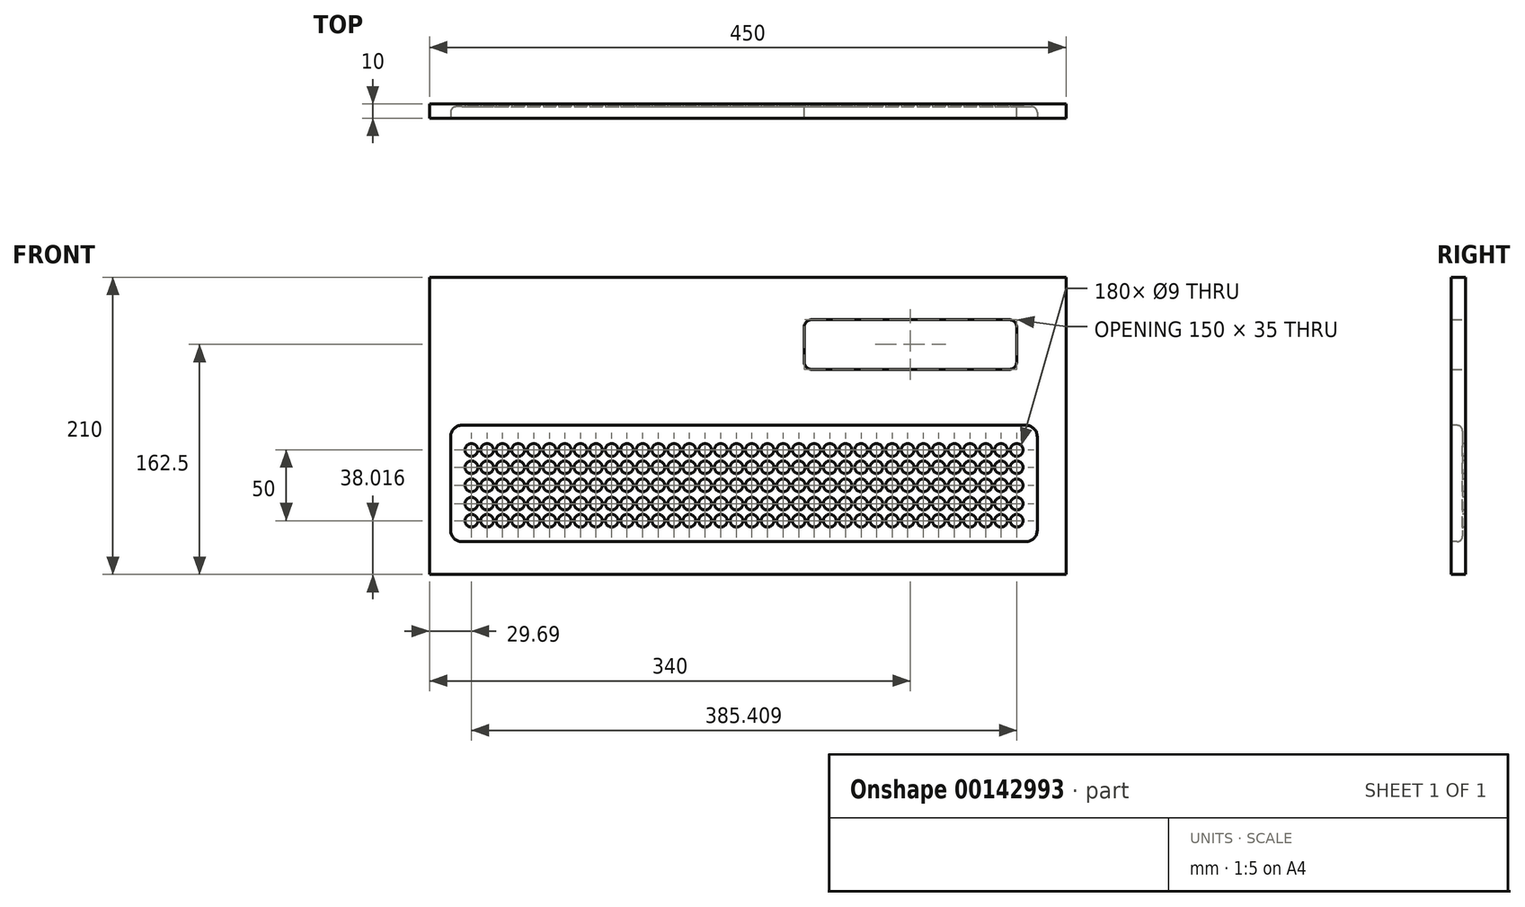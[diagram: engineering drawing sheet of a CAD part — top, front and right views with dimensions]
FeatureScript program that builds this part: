
annotation { "Feature Type Name" : "Feature", "Feature Type Description" : "" }
export const myFeature = defineFeature(function(context is Context, id is Id, definition is map)
    precondition{}
    {
        {
            var Q0;
            Q0=qCreatedBy(makeId("Front.planeOp"),FACE);
            var sketch = newSketch(context, id + "F0", { "sketchPlane" : qUnion([Q0])});
            skLineSegment(sketch, "E0.bottom", {"start": v(0, 0) * mm, "end": v(450, 0) * mm});
            skLineSegment(sketch, "E0.left", {"start": v(0, 0) * mm, "end": v(0, 210) * mm});
            skLineSegment(sketch, "E0.right", {"start": v(450, 0) * mm, "end": v(450, 210) * mm});
            skLineSegment(sketch, "E1.bottom", {"start": v(450, 210) * mm, "end": v(265, 210) * mm});
            skLineSegment(sketch, "E1.top", {"start": v(450, 145) * mm, "end": v(265, 145) * mm, "construction": true});
            skLineSegment(sketch, "E1.right", {"start": v(265, 210) * mm, "end": v(265, 145) * mm, "construction": true});
            skLineSegment(sketch, "E2", {"start": v(0, 210) * mm, "end": v(265, 210) * mm});
            skLineSegment(sketch, "E3.bottom", {"start": v(270, 145) * mm, "end": v(410, 145) * mm});
            skLineSegment(sketch, "E3.top", {"start": v(270, 180) * mm, "end": v(410, 180) * mm});
            skLineSegment(sketch, "E3.left", {"start": v(265, 150) * mm, "end": v(265, 175) * mm});
            skLineSegment(sketch, "E3.right", {"start": v(415, 150) * mm, "end": v(415, 175) * mm});
            skPoint(sketch, "E4.visualSharp", {"position": v(265, 180) * mm});
            skArc(sketch, "E4.filletArc", {"start": v(270, 180) * mm, "mid": v(266.46, 178.54) * mm, "end": v(265, 175) * mm});
            skPoint(sketch, "E5.visualSharp", {"position": v(415, 180) * mm});
            skArc(sketch, "E5.filletArc", {"start": v(415, 175) * mm, "mid": v(413.54, 178.54) * mm, "end": v(410, 180) * mm});
            skPoint(sketch, "E6.visualSharp", {"position": v(415, 145) * mm});
            skArc(sketch, "E6.filletArc", {"start": v(410, 145) * mm, "mid": v(413.54, 146.46) * mm, "end": v(415, 150) * mm});
            skPoint(sketch, "E7.visualSharp", {"position": v(265, 145) * mm});
            skArc(sketch, "E7.filletArc", {"start": v(265, 150) * mm, "mid": v(266.46, 146.46) * mm, "end": v(270, 145) * mm});
            skSolve(sketch);
        }
        {
            var Q0;
            Q0 = qSketchRegion(id + "F0", true);
            extrude(context, id + "F1", {"entities" : qUnion([Q0]), "depth" : 10 * mm, "offsetDistance" : 25 * mm});
        }
        {
            var Q0;
            Q0=makeQuery(id+"F1.opExtrude","CAP_FACE",FACE,{"disambiguationData":[OSD([sQuery(id+"F0.wireOp",EDGE,"E0.bottom"),sQuery(id+"F0.wireOp",EDGE,"E0.top"),sQuery(id+"F0.wireOp",EDGE,"E0.left"),sQuery(id+"F0.wireOp",EDGE,"E0.right")])],"isStart":false});
            var sketch = newSketch(context, id + "F2", { "sketchPlane" : qUnion([Q0])});
            skPoint(sketch, "E8", {"position": v(40.79, 63.02) * mm});
            skPoint(sketch, "E9", {"position": v(40.79, 75.78) * mm});
            skPoint(sketch, "E10", {"position": v(40.79, 88.02) * mm});
            skPoint(sketch, "E11", {"position": v(40.79, 50.08) * mm});
            skPoint(sketch, "E12", {"position": v(29.7, 50.08) * mm});
            skPoint(sketch, "E13", {"position": v(29.7, 63.02) * mm});
            skPoint(sketch, "E14", {"position": v(29.7, 75.78) * mm});
            skPoint(sketch, "E15", {"position": v(29.7, 88.02) * mm});
            skPoint(sketch, "E16", {"position": v(29.7, 38.02) * mm});
            skPoint(sketch, "E17", {"position": v(40.79, 38.02) * mm});
            skPoint(sketch, "E18", {"position": v(130.5, 270.05) * mm});
            skPoint(sketch, "E19.MirrorP", {"position": v(62.7, 88.02) * mm});
            skPoint(sketch, "E20.MirrorP", {"position": v(51.6, 88.02) * mm});
            skPoint(sketch, "E21.MirrorP", {"position": v(62.7, 75.78) * mm});
            skPoint(sketch, "E22.MirrorP", {"position": v(51.6, 75.78) * mm});
            skPoint(sketch, "E23.MirrorP", {"position": v(62.7, 63.02) * mm});
            skPoint(sketch, "E24.MirrorP", {"position": v(51.6, 63.02) * mm});
            skPoint(sketch, "E25.MirrorP", {"position": v(62.7, 50.08) * mm});
            skPoint(sketch, "E26.MirrorP", {"position": v(51.6, 50.08) * mm});
            skPoint(sketch, "E27.MirrorP", {"position": v(62.7, 38.02) * mm});
            skPoint(sketch, "E28.MirrorP", {"position": v(51.6, 38.02) * mm});
            skPoint(sketch, "E29.MirrorP", {"position": v(73.76, 50.08) * mm});
            skPoint(sketch, "E30.MirrorP", {"position": v(73.76, 75.78) * mm});
            skPoint(sketch, "E31.MirrorP", {"position": v(84.86, 88.02) * mm});
            skPoint(sketch, "E32.MirrorP", {"position": v(84.86, 50.08) * mm});
            skPoint(sketch, "E33.MirrorP", {"position": v(95.68, 88.02) * mm});
            skPoint(sketch, "E34.MirrorP", {"position": v(73.76, 38.02) * mm});
            skPoint(sketch, "E35.MirrorP", {"position": v(95.68, 75.78) * mm});
            skPoint(sketch, "E36.MirrorP", {"position": v(95.68, 50.08) * mm});
            skPoint(sketch, "E37.MirrorP", {"position": v(84.86, 38.02) * mm});
            skPoint(sketch, "E38.MirrorP", {"position": v(106.77, 50.08) * mm});
            skPoint(sketch, "E39.MirrorP", {"position": v(95.68, 63.02) * mm});
            skPoint(sketch, "E40.MirrorP", {"position": v(84.86, 75.78) * mm});
            skPoint(sketch, "E41.MirrorP", {"position": v(106.77, 63.02) * mm});
            skPoint(sketch, "E42.MirrorP", {"position": v(73.76, 63.02) * mm});
            skPoint(sketch, "E43.MirrorP", {"position": v(106.77, 75.78) * mm});
            skPoint(sketch, "E44.MirrorP", {"position": v(84.86, 63.02) * mm});
            skPoint(sketch, "E45.MirrorP", {"position": v(106.77, 88.02) * mm});
            skPoint(sketch, "E46.MirrorP", {"position": v(106.77, 38.02) * mm});
            skPoint(sketch, "E47.MirrorP", {"position": v(95.68, 38.02) * mm});
            skPoint(sketch, "E48.MirrorP", {"position": v(73.76, 88.02) * mm});
            skPoint(sketch, "E49.MirrorP", {"position": v(194.84, 38.02) * mm});
            skPoint(sketch, "E50.MirrorP", {"position": v(128.85, 88.02) * mm});
            skPoint(sketch, "E51.MirrorP", {"position": v(194.84, 88.02) * mm});
            skPoint(sketch, "E52.MirrorP", {"position": v(194.84, 75.78) * mm});
            skPoint(sketch, "E53.MirrorP", {"position": v(128.85, 75.78) * mm});
            skPoint(sketch, "E54.MirrorP", {"position": v(172.92, 38.02) * mm});
            skPoint(sketch, "E55.MirrorP", {"position": v(139.67, 63.02) * mm});
            skPoint(sketch, "E56.MirrorP", {"position": v(161.83, 88.02) * mm});
            skPoint(sketch, "E57.MirrorP", {"position": v(194.84, 63.02) * mm});
            skPoint(sketch, "E58.MirrorP", {"position": v(150.76, 75.78) * mm});
            skPoint(sketch, "E59.MirrorP", {"position": v(139.67, 38.02) * mm});
            skPoint(sketch, "E60.MirrorP", {"position": v(117.75, 38.02) * mm});
            skPoint(sketch, "E61.MirrorP", {"position": v(161.83, 63.02) * mm});
            skPoint(sketch, "E62.MirrorP", {"position": v(161.83, 75.78) * mm});
            skPoint(sketch, "E63.MirrorP", {"position": v(128.85, 63.02) * mm});
            skPoint(sketch, "E64.MirrorP", {"position": v(117.75, 63.02) * mm});
            skPoint(sketch, "E65.MirrorP", {"position": v(161.83, 50.08) * mm});
            skPoint(sketch, "E66.MirrorP", {"position": v(117.75, 75.78) * mm});
            skPoint(sketch, "E67.MirrorP", {"position": v(161.83, 38.02) * mm});
            skPoint(sketch, "E68.MirrorP", {"position": v(139.67, 50.08) * mm});
            skPoint(sketch, "E69.MirrorP", {"position": v(150.76, 88.02) * mm});
            skPoint(sketch, "E70.MirrorP", {"position": v(117.75, 88.02) * mm});
            skPoint(sketch, "E71.MirrorP", {"position": v(183.74, 38.02) * mm});
            skPoint(sketch, "E72.MirrorP", {"position": v(183.74, 63.02) * mm});
            skPoint(sketch, "E73.MirrorP", {"position": v(183.74, 75.78) * mm});
            skPoint(sketch, "E74.MirrorP", {"position": v(183.74, 88.02) * mm});
            skPoint(sketch, "E75.MirrorP", {"position": v(183.74, 50.08) * mm});
            skPoint(sketch, "E76.MirrorP", {"position": v(194.84, 50.08) * mm});
            skPoint(sketch, "E77.MirrorP", {"position": v(128.85, 38.02) * mm});
            skPoint(sketch, "E78.MirrorP", {"position": v(139.67, 88.02) * mm});
            skPoint(sketch, "E79.MirrorP", {"position": v(128.85, 50.08) * mm});
            skPoint(sketch, "E80.MirrorP", {"position": v(150.76, 50.08) * mm});
            skPoint(sketch, "E81.MirrorP", {"position": v(150.76, 63.02) * mm});
            skPoint(sketch, "E82.MirrorP", {"position": v(172.92, 50.08) * mm});
            skPoint(sketch, "E83.MirrorP", {"position": v(172.92, 63.02) * mm});
            skPoint(sketch, "E84.MirrorP", {"position": v(139.67, 75.78) * mm});
            skPoint(sketch, "E85.MirrorP", {"position": v(150.76, 38.02) * mm});
            skPoint(sketch, "E86.MirrorP", {"position": v(172.92, 75.78) * mm});
            skPoint(sketch, "E87.MirrorP", {"position": v(117.75, 50.08) * mm});
            skPoint(sketch, "E88.MirrorP", {"position": v(172.92, 88.02) * mm});
            skPoint(sketch, "E89.MirrorP", {"position": v(371.1, 75.78) * mm});
            skPoint(sketch, "E90.MirrorP", {"position": v(305.1, 88.02) * mm});
            skPoint(sketch, "E91.MirrorP", {"position": v(349.18, 50.08) * mm});
            skPoint(sketch, "E92.MirrorP", {"position": v(205.95, 38.02) * mm});
            skPoint(sketch, "E93.MirrorP", {"position": v(217.04, 75.78) * mm});
            skPoint(sketch, "E94.MirrorP", {"position": v(327.02, 63.02) * mm});
            skPoint(sketch, "E95.MirrorP", {"position": v(338.08, 50.08) * mm});
            skPoint(sketch, "E96.MirrorP", {"position": v(294, 63.02) * mm});
            skPoint(sketch, "E97.MirrorP", {"position": v(205.95, 63.02) * mm});
            skPoint(sketch, "E98.MirrorP", {"position": v(327.02, 75.78) * mm});
            skPoint(sketch, "E99.MirrorP", {"position": v(294, 38.02) * mm});
            skPoint(sketch, "E100.MirrorP", {"position": v(238.96, 75.78) * mm});
            skPoint(sketch, "E101.MirrorP", {"position": v(238.96, 50.08) * mm});
            skPoint(sketch, "E102.MirrorP", {"position": v(217.04, 88.02) * mm});
            skPoint(sketch, "E103.MirrorP", {"position": v(217.04, 38.02) * mm});
            skPoint(sketch, "E104.MirrorP", {"position": v(283.03, 50.08) * mm});
            skPoint(sketch, "E105.MirrorP", {"position": v(338.08, 63.02) * mm});
            skPoint(sketch, "E106.MirrorP", {"position": v(371.1, 88.02) * mm});
            skPoint(sketch, "E107.MirrorP", {"position": v(327.02, 38.02) * mm});
            skPoint(sketch, "E108.MirrorP", {"position": v(338.08, 38.02) * mm});
            skPoint(sketch, "E109.MirrorP", {"position": v(294, 75.78) * mm});
            skPoint(sketch, "E110.MirrorP", {"position": v(271.93, 88.02) * mm});
            skPoint(sketch, "E111.MirrorP", {"position": v(305.1, 63.02) * mm});
            skPoint(sketch, "E112.MirrorP", {"position": v(360, 38.02) * mm});
            skPoint(sketch, "E113.MirrorP", {"position": v(205.95, 50.08) * mm});
            skPoint(sketch, "E114.MirrorP", {"position": v(227.86, 63.02) * mm});
            skPoint(sketch, "E115.MirrorP", {"position": v(227.86, 50.08) * mm});
            skPoint(sketch, "E116.MirrorP", {"position": v(283.03, 38.02) * mm});
            skPoint(sketch, "E117.MirrorP", {"position": v(238.96, 38.02) * mm});
            skPoint(sketch, "E118.MirrorP", {"position": v(315.92, 63.02) * mm});
            skPoint(sketch, "E119.MirrorP", {"position": v(294, 50.08) * mm});
            skPoint(sketch, "E120.MirrorP", {"position": v(205.95, 88.02) * mm});
            skPoint(sketch, "E121.MirrorP", {"position": v(349.18, 38.02) * mm});
            skPoint(sketch, "E122.MirrorP", {"position": v(305.1, 75.78) * mm});
            skPoint(sketch, "E123.MirrorP", {"position": v(283.03, 75.78) * mm});
            skPoint(sketch, "E124.MirrorP", {"position": v(360, 50.08) * mm});
            skPoint(sketch, "E125.MirrorP", {"position": v(371.1, 38.02) * mm});
            skPoint(sketch, "E126.MirrorP", {"position": v(371.1, 50.08) * mm});
            skPoint(sketch, "E127.MirrorP", {"position": v(271.93, 38.02) * mm});
            skPoint(sketch, "E128.MirrorP", {"position": v(294, 88.02) * mm});
            skPoint(sketch, "E129.MirrorP", {"position": v(238.96, 63.02) * mm});
            skPoint(sketch, "E130.MirrorP", {"position": v(327.02, 50.08) * mm});
            skPoint(sketch, "E131.MirrorP", {"position": v(338.08, 75.78) * mm});
            skPoint(sketch, "E132.MirrorP", {"position": v(315.92, 50.08) * mm});
            skPoint(sketch, "E133.MirrorP", {"position": v(217.04, 50.08) * mm});
            skPoint(sketch, "E134.MirrorP", {"position": v(349.18, 63.02) * mm});
            skPoint(sketch, "E135.MirrorP", {"position": v(238.96, 88.02) * mm});
            skPoint(sketch, "E136.MirrorP", {"position": v(271.93, 50.08) * mm});
            skPoint(sketch, "E137.MirrorP", {"position": v(371.1, 63.02) * mm});
            skPoint(sketch, "E138.MirrorP", {"position": v(315.92, 75.78) * mm});
            skPoint(sketch, "E139.MirrorP", {"position": v(283.03, 88.02) * mm});
            skPoint(sketch, "E140.MirrorP", {"position": v(271.93, 63.02) * mm});
            skPoint(sketch, "E141.MirrorP", {"position": v(227.86, 88.02) * mm});
            skPoint(sketch, "E142.MirrorP", {"position": v(283.03, 63.02) * mm});
            skPoint(sketch, "E143.MirrorP", {"position": v(305.1, 38.02) * mm});
            skPoint(sketch, "E144.MirrorP", {"position": v(360, 88.02) * mm});
            skPoint(sketch, "E145.MirrorP", {"position": v(315.92, 88.02) * mm});
            skPoint(sketch, "E146.MirrorP", {"position": v(360, 75.78) * mm});
            skPoint(sketch, "E147.MirrorP", {"position": v(271.93, 75.78) * mm});
            skPoint(sketch, "E148.MirrorP", {"position": v(360, 63.02) * mm});
            skPoint(sketch, "E149.MirrorP", {"position": v(338.08, 88.02) * mm});
            skPoint(sketch, "E150.MirrorP", {"position": v(349.18, 75.78) * mm});
            skPoint(sketch, "E151.MirrorP", {"position": v(349.18, 88.02) * mm});
            skPoint(sketch, "E152.MirrorP", {"position": v(315.92, 38.02) * mm});
            skPoint(sketch, "E153.MirrorP", {"position": v(305.1, 50.08) * mm});
            skPoint(sketch, "E154.MirrorP", {"position": v(205.95, 75.78) * mm});
            skPoint(sketch, "E155.MirrorP", {"position": v(327.02, 88.02) * mm});
            skPoint(sketch, "E156.MirrorP", {"position": v(217.04, 63.02) * mm});
            skPoint(sketch, "E157.MirrorP", {"position": v(227.86, 38.02) * mm});
            skPoint(sketch, "E158.MirrorP", {"position": v(227.86, 75.78) * mm});
            skPoint(sketch, "E159.MirrorP", {"position": v(404, 75.78) * mm});
            skPoint(sketch, "E160.MirrorP", {"position": v(393.18, 50.08) * mm});
            skPoint(sketch, "E161.MirrorP", {"position": v(404, 50.08) * mm});
            skPoint(sketch, "E162.MirrorP", {"position": v(393.18, 75.78) * mm});
            skPoint(sketch, "E163.MirrorP", {"position": v(382.09, 63.02) * mm});
            skPoint(sketch, "E164.MirrorP", {"position": v(382.09, 75.78) * mm});
            skPoint(sketch, "E165.MirrorP", {"position": v(393.18, 88.02) * mm});
            skPoint(sketch, "E166.MirrorP", {"position": v(382.09, 38.02) * mm});
            skPoint(sketch, "E167.MirrorP", {"position": v(415.1, 63.02) * mm});
            skPoint(sketch, "E168.MirrorP", {"position": v(415.1, 50.08) * mm});
            skPoint(sketch, "E169.MirrorP", {"position": v(415.1, 38.02) * mm});
            skPoint(sketch, "E170.MirrorP", {"position": v(382.09, 88.02) * mm});
            skPoint(sketch, "E171.MirrorP", {"position": v(404, 63.02) * mm});
            skPoint(sketch, "E172.MirrorP", {"position": v(404, 38.02) * mm});
            skPoint(sketch, "E173.MirrorP", {"position": v(404, 88.02) * mm});
            skPoint(sketch, "E174.MirrorP", {"position": v(415.1, 75.78) * mm});
            skPoint(sketch, "E175.MirrorP", {"position": v(393.18, 63.02) * mm});
            skPoint(sketch, "E176.MirrorP", {"position": v(393.18, 38.02) * mm});
            skPoint(sketch, "E177.MirrorP", {"position": v(382.09, 50.08) * mm});
            skPoint(sketch, "E178.MirrorP", {"position": v(415.1, 88.02) * mm});
            skPoint(sketch, "E179.MirrorP", {"position": v(261.12, 88.02) * mm});
            skPoint(sketch, "E180.MirrorP", {"position": v(250.02, 38.02) * mm});
            skPoint(sketch, "E181.MirrorP", {"position": v(261.12, 75.78) * mm});
            skPoint(sketch, "E182.MirrorP", {"position": v(250.02, 75.78) * mm});
            skPoint(sketch, "E183.MirrorP", {"position": v(250.02, 63.02) * mm});
            skPoint(sketch, "E184.MirrorP", {"position": v(261.12, 63.02) * mm});
            skPoint(sketch, "E185.MirrorP", {"position": v(261.12, 38.02) * mm});
            skPoint(sketch, "E186.MirrorP", {"position": v(261.12, 50.08) * mm});
            skPoint(sketch, "E187.MirrorP", {"position": v(250.02, 50.08) * mm});
            skPoint(sketch, "E188.MirrorP", {"position": v(250.02, 88.02) * mm});
            skSolve(sketch);
        }
        {
            var Q0;
            Q0=sQuery(id+"F2.wireOp",VERTEX,"E66.MirrorP");
            var Q1;
            Q1=sQuery(id+"F2.wireOp",VERTEX,"E50.MirrorP");
            var Q2;
            Q2=sQuery(id+"F2.wireOp",VERTEX,"E34.MirrorP");
            var Q3;
            Q3=sQuery(id+"F2.wireOp",VERTEX,"E82.MirrorP");
            var Q4;
            Q4=sQuery(id+"F2.wireOp",VERTEX,"E28.MirrorP");
            var Q5;
            Q5=sQuery(id+"F2.wireOp",VERTEX,"E85.MirrorP");
            var Q6;
            Q6=sQuery(id+"F2.wireOp",VERTEX,"E69.MirrorP");
            var Q7;
            Q7=sQuery(id+"F2.wireOp",VERTEX,"E53.MirrorP");
            var Q8;
            Q8=sQuery(id+"F2.wireOp",VERTEX,"E60.MirrorP");
            var Q9;
            Q9=sQuery(id+"F2.wireOp",VERTEX,"E37.MirrorP");
            var Q10;
            Q10=sQuery(id+"F2.wireOp",VERTEX,"E44.MirrorP");
            var Q11;
            Q11=sQuery(id+"F2.wireOp",VERTEX,"E67.MirrorP");
            var Q12;
            Q12=sQuery(id+"F2.wireOp",VERTEX,"E35.MirrorP");
            var Q13;
            Q13=sQuery(id+"F2.wireOp",VERTEX,"E83.MirrorP");
            var Q14;
            Q14=sQuery(id+"F2.wireOp",VERTEX,"E29.MirrorP");
            var Q15;
            Q15=sQuery(id+"F2.wireOp",VERTEX,"E86.MirrorP");
            var Q16;
            Q16=sQuery(id+"F2.wireOp",VERTEX,"E70.MirrorP");
            var Q17;
            Q17=sQuery(id+"F2.wireOp",VERTEX,"E77.MirrorP");
            var Q18;
            Q18=sQuery(id+"F2.wireOp",VERTEX,"E54.MirrorP");
            var Q19;
            Q19=sQuery(id+"F2.wireOp",VERTEX,"E61.MirrorP");
            var Q20;
            Q20=sQuery(id+"F2.wireOp",VERTEX,"E38.MirrorP");
            var Q21;
            Q21=sQuery(id+"F2.wireOp",VERTEX,"E45.MirrorP");
            var Q22;
            Q22=sQuery(id+"F2.wireOp",VERTEX,"E8");
            var Q23;
            Q23=sQuery(id+"F2.wireOp",VERTEX,"E23.MirrorP");
            var Q24;
            Q24=sQuery(id+"F2.wireOp",VERTEX,"E78.MirrorP");
            var Q25;
            Q25=sQuery(id+"F2.wireOp",VERTEX,"E87.MirrorP");
            var Q26;
            Q26=sQuery(id+"F2.wireOp",VERTEX,"E55.MirrorP");
            var Q27;
            Q27=sQuery(id+"F2.wireOp",VERTEX,"E39.MirrorP");
            var Q28;
            Q28=sQuery(id+"F2.wireOp",VERTEX,"E62.MirrorP");
            var Q29;
            Q29=sQuery(id+"F2.wireOp",VERTEX,"E46.MirrorP");
            var Q30;
            Q30=sQuery(id+"F2.wireOp",VERTEX,"E30.MirrorP");
            var Q31;
            Q31=sQuery(id+"F2.wireOp",VERTEX,"E24.MirrorP");
            var Q32;
            Q32=sQuery(id+"F2.wireOp",VERTEX,"E88.MirrorP");
            var Q33;
            Q33=sQuery(id+"F2.wireOp",VERTEX,"E56.MirrorP");
            var Q34;
            Q34=sQuery(id+"F2.wireOp",VERTEX,"E40.MirrorP");
            var Q35;
            Q35=sQuery(id+"F2.wireOp",VERTEX,"E63.MirrorP");
            var Q36;
            Q36=sQuery(id+"F2.wireOp",VERTEX,"E47.MirrorP");
            var Q37;
            Q37=sQuery(id+"F2.wireOp",VERTEX,"E31.MirrorP");
            var Q38;
            Q38=sQuery(id+"F2.wireOp",VERTEX,"E79.MirrorP");
            var Q39;
            Q39=sQuery(id+"F2.wireOp",VERTEX,"E20.MirrorP");
            var Q40;
            Q40=sQuery(id+"F2.wireOp",VERTEX,"E25.MirrorP");
            var Q41;
            Q41=sQuery(id+"F2.wireOp",VERTEX,"E21.MirrorP");
            var Q42;
            Q42=sQuery(id+"F2.wireOp",VERTEX,"E22.MirrorP");
            var Q43;
            Q43=sQuery(id+"F2.wireOp",VERTEX,"E41.MirrorP");
            var Q44;
            Q44=sQuery(id+"F2.wireOp",VERTEX,"E9");
            var Q45;
            Q45=sQuery(id+"F2.wireOp",VERTEX,"E10");
            var Q46;
            Q46=sQuery(id+"F2.wireOp",VERTEX,"E11");
            var Q47;
            Q47=sQuery(id+"F2.wireOp",VERTEX,"E12");
            var Q48;
            Q48=sQuery(id+"F2.wireOp",VERTEX,"E13");
            var Q49;
            Q49=sQuery(id+"F2.wireOp",VERTEX,"E14");
            var Q50;
            Q50=sQuery(id+"F2.wireOp",VERTEX,"E15");
            var Q51;
            Q51=sQuery(id+"F2.wireOp",VERTEX,"E16");
            var Q52;
            Q52=sQuery(id+"F2.wireOp",VERTEX,"E17");
            var Q53;
            Q53=sQuery(id+"F2.wireOp",VERTEX,"E19.MirrorP");
            var Q54;
            Q54=sQuery(id+"F2.wireOp",VERTEX,"E64.MirrorP");
            var Q55;
            Q55=sQuery(id+"F2.wireOp",VERTEX,"E48.MirrorP");
            var Q56;
            Q56=sQuery(id+"F2.wireOp",VERTEX,"E32.MirrorP");
            var Q57;
            Q57=sQuery(id+"F2.wireOp",VERTEX,"E80.MirrorP");
            var Q58;
            Q58=sQuery(id+"F2.wireOp",VERTEX,"E26.MirrorP");
            var Q59;
            Q59=sQuery(id+"F2.wireOp",VERTEX,"E58.MirrorP");
            var Q60;
            Q60=sQuery(id+"F2.wireOp",VERTEX,"E42.MirrorP");
            var Q61;
            Q61=sQuery(id+"F2.wireOp",VERTEX,"E65.MirrorP");
            var Q62;
            Q62=sQuery(id+"F2.wireOp",VERTEX,"E33.MirrorP");
            var Q63;
            Q63=sQuery(id+"F2.wireOp",VERTEX,"E81.MirrorP");
            var Q64;
            Q64=sQuery(id+"F2.wireOp",VERTEX,"E27.MirrorP");
            var Q65;
            Q65=sQuery(id+"F2.wireOp",VERTEX,"E84.MirrorP");
            var Q66;
            Q66=sQuery(id+"F2.wireOp",VERTEX,"E68.MirrorP");
            var Q67;
            Q67=sQuery(id+"F2.wireOp",VERTEX,"E59.MirrorP");
            var Q68;
            Q68=sQuery(id+"F2.wireOp",VERTEX,"E36.MirrorP");
            var Q69;
            Q69=sQuery(id+"F2.wireOp",VERTEX,"E43.MirrorP");
            var Q70;
            Q70=sQuery(id+"F2.wireOp",VERTEX,"E74.MirrorP");
            var Q71;
            Q71=sQuery(id+"F2.wireOp",VERTEX,"E51.MirrorP");
            var Q72;
            Q72=sQuery(id+"F2.wireOp",VERTEX,"E120.MirrorP");
            var Q73;
            Q73=sQuery(id+"F2.wireOp",VERTEX,"E102.MirrorP");
            var Q74;
            Q74=sQuery(id+"F2.wireOp",VERTEX,"E141.MirrorP");
            var Q75;
            Q75=sQuery(id+"F2.wireOp",VERTEX,"E135.MirrorP");
            var Q76;
            Q76=sQuery(id+"F2.wireOp",VERTEX,"E76.MirrorP");
            var Q77;
            Q77=sQuery(id+"F2.wireOp",VERTEX,"E114.MirrorP");
            var Q78;
            Q78=sQuery(id+"F2.wireOp",VERTEX,"E97.MirrorP");
            var Q79;
            Q79=sQuery(id+"F2.wireOp",VERTEX,"E100.MirrorP");
            var Q80;
            Q80=sQuery(id+"F2.wireOp",VERTEX,"E103.MirrorP");
            var Q81;
            Q81=sQuery(id+"F2.wireOp",VERTEX,"E75.MirrorP");
            var Q82;
            Q82=sQuery(id+"F2.wireOp",VERTEX,"E101.MirrorP");
            var Q83;
            Q83=sQuery(id+"F2.wireOp",VERTEX,"E49.MirrorP");
            var Q84;
            Q84=sQuery(id+"F2.wireOp",VERTEX,"E158.MirrorP");
            var Q85;
            Q85=sQuery(id+"F2.wireOp",VERTEX,"E129.MirrorP");
            var Q86;
            Q86=sQuery(id+"F2.wireOp",VERTEX,"E157.MirrorP");
            var Q87;
            Q87=sQuery(id+"F2.wireOp",VERTEX,"E73.MirrorP");
            var Q88;
            Q88=sQuery(id+"F2.wireOp",VERTEX,"E57.MirrorP");
            var Q89;
            Q89=sQuery(id+"F2.wireOp",VERTEX,"E92.MirrorP");
            var Q90;
            Q90=sQuery(id+"F2.wireOp",VERTEX,"E52.MirrorP");
            var Q91;
            Q91=sQuery(id+"F2.wireOp",VERTEX,"E154.MirrorP");
            var Q92;
            Q92=sQuery(id+"F2.wireOp",VERTEX,"E115.MirrorP");
            var Q93;
            Q93=sQuery(id+"F2.wireOp",VERTEX,"E113.MirrorP");
            var Q94;
            Q94=sQuery(id+"F2.wireOp",VERTEX,"E72.MirrorP");
            var Q95;
            Q95=sQuery(id+"F2.wireOp",VERTEX,"E117.MirrorP");
            var Q96;
            Q96=sQuery(id+"F2.wireOp",VERTEX,"E71.MirrorP");
            var Q97;
            Q97=sQuery(id+"F2.wireOp",VERTEX,"E93.MirrorP");
            var Q98;
            Q98=sQuery(id+"F2.wireOp",VERTEX,"E133.MirrorP");
            var Q99;
            Q99=sQuery(id+"F2.wireOp",VERTEX,"E156.MirrorP");
            var Q100;
            Q100=makeQuery(id+"F1.opExtrude","SWEPT_BODY",BODY,{"disambiguationData":[OSD([sQuery(id+"F0.wireOp",EDGE,"E0.bottom"),sQuery(id+"F0.wireOp",EDGE,"E0.top"),sQuery(id+"F0.wireOp",EDGE,"E0.left"),sQuery(id+"F0.wireOp",EDGE,"E0.right")])]});
            hole(context, id + "F3", {"style" : HoleStyle.SIMPLE, "endStyle" : HoleEndStyle.THROUGH, "holeDiameter" : 9 * mm, "locations" : qUnion([Q0, Q1, Q2, Q3, Q4, Q5, Q6, Q7, Q8, Q9, Q10, Q11, Q12, Q13, Q14, Q15, Q16, Q17, Q18, Q19, Q20, Q21, Q22, Q23, Q24, Q25, Q26, Q27, Q28, Q29, Q30, Q31, Q32, Q33, Q34, Q35, Q36, Q37, Q38, Q39, Q40, Q41, Q42, Q43, Q44, Q45, Q46, Q47, Q48, Q49, Q50, Q51, Q52, Q53, Q54, Q55, Q56, Q57, Q58, Q59, Q60, Q61, Q62, Q63, Q64, Q65, Q66, Q67, Q68, Q69, Q70, Q71, Q72, Q73, Q74, Q75, Q76, Q77, Q78, Q79, Q80, Q81, Q82, Q83, Q84, Q85, Q86, Q87, Q88, Q89, Q90, Q91, Q92, Q93, Q94, Q95, Q96, Q97, Q98, Q99]), "scope" : qUnion([Q100]), "isTappedThrough" : true});
        }
        {
            var Q0;
            Q0=sQuery(id+"F2.wireOp",VERTEX,"E151.MirrorP");
            var Q1;
            Q1=sQuery(id+"F2.wireOp",VERTEX,"E184.MirrorP");
            var Q2;
            Q2=sQuery(id+"F2.wireOp",VERTEX,"1317591f-df84-4e3a-b4a8-ee8bbe8225826.MirrorP");
            var Q3;
            Q3=sQuery(id+"F2.wireOp",VERTEX,"E142.MirrorP");
            var Q4;
            Q4=sQuery(id+"F2.wireOp",VERTEX,"1317591f-df84-4e3a-b4a8-ee8bbe82258260.MirrorP");
            var Q5;
            Q5=sQuery(id+"F2.wireOp",VERTEX,"E106.MirrorP");
            var Q6;
            Q6=sQuery(id+"F2.wireOp",VERTEX,"E127.MirrorP");
            var Q7;
            Q7=sQuery(id+"F2.wireOp",VERTEX,"E145.MirrorP");
            var Q8;
            Q8=sQuery(id+"F2.wireOp",VERTEX,"E172.MirrorP");
            var Q9;
            Q9=sQuery(id+"F2.wireOp",VERTEX,"E171.MirrorP");
            var Q10;
            Q10=sQuery(id+"F2.wireOp",VERTEX,"1317591f-df84-4e3a-b4a8-ee8bbe82258212.MirrorP");
            var Q11;
            Q11=sQuery(id+"F2.wireOp",VERTEX,"E161.MirrorP");
            var Q12;
            Q12=sQuery(id+"F2.wireOp",VERTEX,"E138.MirrorP");
            var Q13;
            Q13=sQuery(id+"F2.wireOp",VERTEX,"E149.MirrorP");
            var Q14;
            Q14=sQuery(id+"F2.wireOp",VERTEX,"E150.MirrorP");
            var Q15;
            Q15=sQuery(id+"F2.wireOp",VERTEX,"E173.MirrorP");
            var Q16;
            Q16=sQuery(id+"F2.wireOp",VERTEX,"E167.MirrorP");
            var Q17;
            Q17=sQuery(id+"F2.wireOp",VERTEX,"E105.MirrorP");
            var Q18;
            Q18=sQuery(id+"F2.wireOp",VERTEX,"1317591f-df84-4e3a-b4a8-ee8bbe8225827.MirrorP");
            var Q19;
            Q19=sQuery(id+"F2.wireOp",VERTEX,"1317591f-df84-4e3a-b4a8-ee8bbe82258219.MirrorP");
            var Q20;
            Q20=sQuery(id+"F2.wireOp",VERTEX,"E153.MirrorP");
            var Q21;
            Q21=sQuery(id+"F2.wireOp",VERTEX,"E126.MirrorP");
            var Q22;
            Q22=sQuery(id+"F2.wireOp",VERTEX,"E112.MirrorP");
            var Q23;
            Q23=sQuery(id+"F2.wireOp",VERTEX,"E168.MirrorP");
            var Q24;
            Q24=sQuery(id+"F2.wireOp",VERTEX,"1317591f-df84-4e3a-b4a8-ee8bbe82258224.MirrorP");
            var Q25;
            Q25=sQuery(id+"F2.wireOp",VERTEX,"1317591f-df84-4e3a-b4a8-ee8bbe82258248.MirrorP");
            var Q26;
            Q26=sQuery(id+"F2.wireOp",VERTEX,"E128.MirrorP");
            var Q27;
            Q27=sQuery(id+"F2.wireOp",VERTEX,"E159.MirrorP");
            var Q28;
            Q28=sQuery(id+"F2.wireOp",VERTEX,"E175.MirrorP");
            var Q29;
            Q29=sQuery(id+"F2.wireOp",VERTEX,"1317591f-df84-4e3a-b4a8-ee8bbe8225824.MirrorP");
            var Q30;
            Q30=sQuery(id+"F2.wireOp",VERTEX,"E174.MirrorP");
            var Q31;
            Q31=sQuery(id+"F2.wireOp",VERTEX,"E107.MirrorP");
            var Q32;
            Q32=sQuery(id+"F2.wireOp",VERTEX,"E119.MirrorP");
            var Q33;
            Q33=sQuery(id+"F2.wireOp",VERTEX,"E179.MirrorP");
            var Q34;
            Q34=sQuery(id+"F2.wireOp",VERTEX,"E187.MirrorP");
            var Q35;
            Q35=sQuery(id+"F2.wireOp",VERTEX,"E1598.MirrorP");
            var Q36;
            Q36=sQuery(id+"F2.wireOp",VERTEX,"1317591f-df84-4e3a-b4a8-ee8bbe82258227.MirrorP");
            var Q37;
            Q37=sQuery(id+"F2.wireOp",VERTEX,"E104.MirrorP");
            var Q38;
            Q38=sQuery(id+"F2.wireOp",VERTEX,"E163.MirrorP");
            var Q39;
            Q39=sQuery(id+"F2.wireOp",VERTEX,"E108.MirrorP");
            var Q40;
            Q40=sQuery(id+"F2.wireOp",VERTEX,"E91.MirrorP");
            var Q41;
            Q41=sQuery(id+"F2.wireOp",VERTEX,"E182.MirrorP");
            var Q42;
            Q42=sQuery(id+"F2.wireOp",VERTEX,"E186.MirrorP");
            var Q43;
            Q43=sQuery(id+"F2.wireOp",VERTEX,"E144.MirrorP");
            var Q44;
            Q44=sQuery(id+"F2.wireOp",VERTEX,"E143.MirrorP");
            var Q45;
            Q45=sQuery(id+"F2.wireOp",VERTEX,"E166.MirrorP");
            var Q46;
            Q46=sQuery(id+"F2.wireOp",VERTEX,"E94.MirrorP");
            var Q47;
            Q47=sQuery(id+"F2.wireOp",VERTEX,"1317591f-df84-4e3a-b4a8-ee8bbe82258217.MirrorP");
            var Q48;
            Q48=sQuery(id+"F2.wireOp",VERTEX,"E136.MirrorP");
            var Q49;
            Q49=sQuery(id+"F2.wireOp",VERTEX,"E98.MirrorP");
            var Q50;
            Q50=sQuery(id+"F2.wireOp",VERTEX,"E148.MirrorP");
            var Q51;
            Q51=sQuery(id+"F2.wireOp",VERTEX,"E96.MirrorP");
            var Q52;
            Q52=sQuery(id+"F2.wireOp",VERTEX,"E178.MirrorP");
            var Q53;
            Q53=sQuery(id+"F2.wireOp",VERTEX,"E109.MirrorP");
            var Q54;
            Q54=sQuery(id+"F2.wireOp",VERTEX,"E118.MirrorP");
            var Q55;
            Q55=sQuery(id+"F2.wireOp",VERTEX,"E177.MirrorP");
            var Q56;
            Q56=sQuery(id+"F2.wireOp",VERTEX,"E183.MirrorP");
            var Q57;
            Q57=sQuery(id+"F2.wireOp",VERTEX,"E89.MirrorP");
            var Q58;
            Q58=sQuery(id+"F2.wireOp",VERTEX,"E130.MirrorP");
            var Q59;
            Q59=sQuery(id+"F2.wireOp",VERTEX,"E95.MirrorP");
            var Q60;
            Q60=sQuery(id+"F2.wireOp",VERTEX,"E152.MirrorP");
            var Q61;
            Q61=sQuery(id+"F2.wireOp",VERTEX,"E146.MirrorP");
            var Q62;
            Q62=sQuery(id+"F2.wireOp",VERTEX,"E1593.MirrorP");
            var Q63;
            Q63=sQuery(id+"F2.wireOp",VERTEX,"E160.MirrorP");
            var Q64;
            Q64=sQuery(id+"F2.wireOp",VERTEX,"E132.MirrorP");
            var Q65;
            Q65=sQuery(id+"F2.wireOp",VERTEX,"E155.MirrorP");
            var Q66;
            Q66=sQuery(id+"F2.wireOp",VERTEX,"E188.MirrorP");
            var Q67;
            Q67=sQuery(id+"F2.wireOp",VERTEX,"E122.MirrorP");
            var Q68;
            Q68=sQuery(id+"F2.wireOp",VERTEX,"E1590.MirrorP");
            var Q69;
            Q69=sQuery(id+"F2.wireOp",VERTEX,"E134.MirrorP");
            var Q70;
            Q70=sQuery(id+"F2.wireOp",VERTEX,"E125.MirrorP");
            var Q71;
            Q71=sQuery(id+"F2.wireOp",VERTEX,"E162.MirrorP");
            var Q72;
            Q72=sQuery(id+"F2.wireOp",VERTEX,"E139.MirrorP");
            var Q73;
            Q73=sQuery(id+"F2.wireOp",VERTEX,"E137.MirrorP");
            var Q74;
            Q74=sQuery(id+"F2.wireOp",VERTEX,"E116.MirrorP");
            var Q75;
            Q75=sQuery(id+"F2.wireOp",VERTEX,"E90.MirrorP");
            var Q76;
            Q76=sQuery(id+"F2.wireOp",VERTEX,"E111.MirrorP");
            var Q77;
            Q77=sQuery(id+"F2.wireOp",VERTEX,"E185.MirrorP");
            var Q78;
            Q78=sQuery(id+"F2.wireOp",VERTEX,"E123.MirrorP");
            var Q79;
            Q79=sQuery(id+"F2.wireOp",VERTEX,"E1597.MirrorP");
            var Q80;
            Q80=sQuery(id+"F2.wireOp",VERTEX,"E181.MirrorP");
            var Q81;
            Q81=sQuery(id+"F2.wireOp",VERTEX,"E99.MirrorP");
            var Q82;
            Q82=sQuery(id+"F2.wireOp",VERTEX,"E110.MirrorP");
            var Q83;
            Q83=sQuery(id+"F2.wireOp",VERTEX,"E164.MirrorP");
            var Q84;
            Q84=sQuery(id+"F2.wireOp",VERTEX,"E121.MirrorP");
            var Q85;
            Q85=sQuery(id+"F2.wireOp",VERTEX,"E147.MirrorP");
            var Q86;
            Q86=sQuery(id+"F2.wireOp",VERTEX,"1317591f-df84-4e3a-b4a8-ee8bbe8225828.MirrorP");
            var Q87;
            Q87=sQuery(id+"F2.wireOp",VERTEX,"E170.MirrorP");
            var Q88;
            Q88=sQuery(id+"F2.wireOp",VERTEX,"E180.MirrorP");
            var Q89;
            Q89=sQuery(id+"F2.wireOp",VERTEX,"E131.MirrorP");
            var Q90;
            Q90=sQuery(id+"F2.wireOp",VERTEX,"E169.MirrorP");
            var Q91;
            Q91=sQuery(id+"F2.wireOp",VERTEX,"E165.MirrorP");
            var Q92;
            Q92=sQuery(id+"F2.wireOp",VERTEX,"E176.MirrorP");
            var Q93;
            Q93=sQuery(id+"F2.wireOp",VERTEX,"E124.MirrorP");
            var Q94;
            Q94=sQuery(id+"F2.wireOp",VERTEX,"E140.MirrorP");
            var Q95;
            Q95=makeQuery(id+"F1.opExtrude","SWEPT_BODY",BODY,{"disambiguationData":[OSD([sQuery(id+"F0.wireOp",EDGE,"E0.bottom"),sQuery(id+"F0.wireOp",EDGE,"E0.top"),sQuery(id+"F0.wireOp",EDGE,"E0.left"),sQuery(id+"F0.wireOp",EDGE,"E0.right")])]});
            hole(context, id + "F4", {"style" : HoleStyle.SIMPLE, "endStyle" : HoleEndStyle.THROUGH, "holeDiameter" : 9 * mm, "locations" : qUnion([Q0, Q1, Q2, Q3, Q4, Q5, Q6, Q7, Q8, Q9, Q10, Q11, Q12, Q13, Q14, Q15, Q16, Q17, Q18, Q19, Q20, Q21, Q22, Q23, Q24, Q25, Q26, Q27, Q28, Q29, Q30, Q31, Q32, Q33, Q34, Q35, Q36, Q37, Q38, Q39, Q40, Q41, Q42, Q43, Q44, Q45, Q46, Q47, Q48, Q49, Q50, Q51, Q52, Q53, Q54, Q55, Q56, Q57, Q58, Q59, Q60, Q61, Q62, Q63, Q64, Q65, Q66, Q67, Q68, Q69, Q70, Q71, Q72, Q73, Q74, Q75, Q76, Q77, Q78, Q79, Q80, Q81, Q82, Q83, Q84, Q85, Q86, Q87, Q88, Q89, Q90, Q91, Q92, Q93, Q94]), "scope" : qUnion([Q95]), "isTappedThrough" : true});
        }
        {
            var Q0;
            Q0=makeQuery(id+"F2.imprint","IMPRINT",FACE,{"disambiguationData":[TD([[makeQuery(id+"F2.imprint","IMPRINT",EDGE,{"derivedFrom":makeQuery(id+"F1.opExtrude","CAP_EDGE",EDGE,{"disambiguationData":[OSD([sQuery(id+"F0.wireOp",EDGE,"E0.bottom")])],"isStart":false})}),1.0]])]});
            var sketch = newSketch(context, id + "F5", { "sketchPlane" : qUnion([Q0])});
            skLineSegment(sketch, "E189.bottom", {"start": v(23, 105.4) * mm, "end": v(421.6, 105.4) * mm});
            skLineSegment(sketch, "E189.top", {"start": v(23, 23.14) * mm, "end": v(421.6, 23.14) * mm});
            skLineSegment(sketch, "E189.left", {"start": v(15, 97.4) * mm, "end": v(15, 31.14) * mm});
            skLineSegment(sketch, "E189.right", {"start": v(429.6, 97.4) * mm, "end": v(429.6, 31.14) * mm});
            skPoint(sketch, "E190.visualSharp", {"position": v(15, 105.4) * mm});
            skArc(sketch, "E190.filletArc", {"start": v(23, 105.4) * mm, "mid": v(17.35, 103.07) * mm, "end": v(15, 97.4) * mm});
            skPoint(sketch, "E191.visualSharp", {"position": v(15, 23.14) * mm});
            skArc(sketch, "E191.filletArc", {"start": v(15, 31.14) * mm, "mid": v(17.35, 25.48) * mm, "end": v(23, 23.14) * mm});
            skPoint(sketch, "E192.visualSharp", {"position": v(429.6, 105.4) * mm});
            skArc(sketch, "E192.filletArc", {"start": v(429.6, 97.4) * mm, "mid": v(427.27, 103.07) * mm, "end": v(421.6, 105.4) * mm});
            skPoint(sketch, "E193.visualSharp", {"position": v(429.6, 23.14) * mm});
            skArc(sketch, "E193.filletArc", {"start": v(421.6, 23.14) * mm, "mid": v(427.27, 25.48) * mm, "end": v(429.6, 31.14) * mm});
            skSolve(sketch);
        }
        {
            var Q0;
            Q0 = qSketchRegion(id + "F5", true);
            extrude(context, id + "F6", {"entities" : qUnion([Q0]), "operationType" : NewBodyOperationType.REMOVE, "oppositeDirection" : true, "depth" : 8 * mm});
        }
        {
            var Q0;
            Q0=makeQuery(id+"F6.boolean.opBoolean","COPY",EDGE,{"derivedFrom":makeQuery(id+"F6.opExtrude","CAP_EDGE",EDGE,{"disambiguationData":[OSD([sQuery(id+"F5.wireOp",EDGE,"E189.bottom")])],"isStart":true})});
            var Q1;
            Q1=makeQuery(id+"F6.boolean.opBoolean","COPY",EDGE,{"derivedFrom":makeQuery(id+"F6.opExtrude","CAP_EDGE",EDGE,{"disambiguationData":[OSD([sQuery(id+"F5.wireOp",EDGE,"E190.filletArc")])],"isStart":true})});
            var Q2;
            Q2=makeQuery(id+"F6.boolean.opBoolean","COPY",EDGE,{"derivedFrom":makeQuery(id+"F6.opExtrude","CAP_EDGE",EDGE,{"disambiguationData":[OSD([sQuery(id+"F5.wireOp",EDGE,"E189.left")])],"isStart":true})});
            var Q3;
            Q3=makeQuery(id+"F6.boolean.opBoolean","COPY",EDGE,{"derivedFrom":makeQuery(id+"F6.opExtrude","CAP_EDGE",EDGE,{"disambiguationData":[OSD([sQuery(id+"F5.wireOp",EDGE,"E191.filletArc")])],"isStart":true})});
            var Q4;
            Q4=makeQuery(id+"F6.boolean.opBoolean","COPY",EDGE,{"derivedFrom":makeQuery(id+"F6.opExtrude","CAP_EDGE",EDGE,{"disambiguationData":[OSD([sQuery(id+"F5.wireOp",EDGE,"E189.top")])],"isStart":true})});
            var Q5;
            Q5=makeQuery(id+"F6.boolean.opBoolean","COPY",EDGE,{"derivedFrom":makeQuery(id+"F6.opExtrude","CAP_EDGE",EDGE,{"disambiguationData":[OSD([sQuery(id+"F5.wireOp",EDGE,"E193.filletArc")])],"isStart":true})});
            var Q6;
            Q6=makeQuery(id+"F6.boolean.opBoolean","COPY",EDGE,{"derivedFrom":makeQuery(id+"F6.opExtrude","CAP_EDGE",EDGE,{"disambiguationData":[OSD([sQuery(id+"F5.wireOp",EDGE,"E189.right")])],"isStart":true})});
            var Q7;
            Q7=makeQuery(id+"F6.boolean.opBoolean","COPY",EDGE,{"derivedFrom":makeQuery(id+"F6.opExtrude","CAP_EDGE",EDGE,{"disambiguationData":[OSD([sQuery(id+"F5.wireOp",EDGE,"E192.filletArc")])],"isStart":true})});
            var Q8;
            Q8=makeQuery(id+"F6.boolean.opBoolean","COPY",EDGE,{"derivedFrom":makeQuery(id+"F6.opExtrude","CAP_EDGE",EDGE,{"disambiguationData":[OSD([sQuery(id+"F5.wireOp",EDGE,"E189.left")])],"isStart":false})});
            var Q9;
            Q9=makeQuery(id+"F6.boolean.opBoolean","COPY",EDGE,{"derivedFrom":makeQuery(id+"F6.opExtrude","CAP_EDGE",EDGE,{"disambiguationData":[OSD([sQuery(id+"F5.wireOp",EDGE,"E190.filletArc")])],"isStart":false})});
            var Q10;
            Q10=makeQuery(id+"F6.boolean.opBoolean","COPY",EDGE,{"derivedFrom":makeQuery(id+"F6.opExtrude","CAP_EDGE",EDGE,{"disambiguationData":[OSD([sQuery(id+"F5.wireOp",EDGE,"E189.bottom")])],"isStart":false})});
            fillet(context, id + "F7", {"entities" : qUnion([Q0, Q1, Q2, Q3, Q4, Q5, Q6, Q7, Q8, Q9, Q10]), "radius" : 4 * mm, "tangentPropagation" : true, "allowEdgeOverflow" : false});
        }
    });
